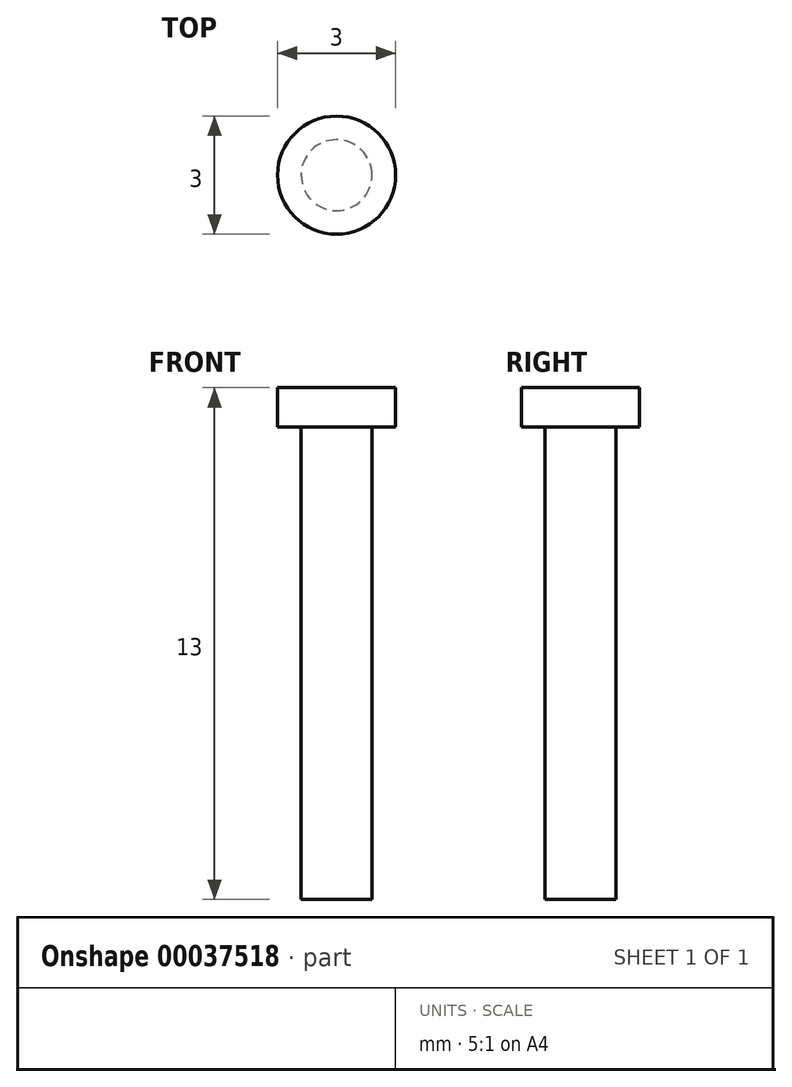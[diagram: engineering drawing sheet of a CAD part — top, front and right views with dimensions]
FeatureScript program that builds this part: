
annotation { "Feature Type Name" : "Feature", "Feature Type Description" : "" }
export const myFeature = defineFeature(function(context is Context, id is Id, definition is map)
    precondition{}
    {
        {
            var Q0;
            Q0=qCreatedBy(makeId("Top.planeOp"),FACE);
            var sketch = newSketch(context, id + "F0", { "sketchPlane" : qUnion([Q0])});
            skCircle(sketch, "E0", {"center": v(0, 0) * mm, "radius": 1.5 * mm});
            skCircle(sketch, "E1", {"center": v(0, 0) * mm, "radius": 0.9 * mm});
            skSolve(sketch);
        }
        {
            var Q0;
            Q0=makeQuery(id+"F0.imprint","IMPRINT",FACE,{"disambiguationData":[TD([[makeQuery(id+"F0.imprint","IMPRINT",EDGE,{"derivedFrom":sQuery(id+"F0.wireOp",EDGE,"E1")}),1.0]])]});
            var Q1;
            Q1=sQuery(id+"F0.wireOp",EDGE,"E1");
            extrude(context, id + "F1", {"entities" : qUnion([Q0]), "surfaceEntities" : qUnion([Q1]), "oppositeDirection" : true, "depth" : 12 * mm});
        }
        {
            var Q0;
            Q0=qSketchRegion(id+"F0",true);
            extrude(context, id + "F2", {"entities" : qUnion([Q0]), "depth" : 1 * mm});
        }
        {
            var Q0;
            Q0=makeQuery(id+"F1.opExtrude","CAP_FACE",FACE,{"disambiguationData":[OSD([sQuery(id+"F0.wireOp",EDGE,"E1")])],"isStart":true});
            var Q1;
            Q1=makeQuery(id+"F2.opExtrude","CAP_FACE",FACE,{"disambiguationData":[OSD([sQuery(id+"F0.wireOp",EDGE,"E0"),sQuery(id+"F0.wireOp",EDGE,"E1")])],"isStart":false});
            extrude(context, id + "F3", {"entities" : qUnion([Q0]), "operationType" : NewBodyOperationType.ADD, "endBound" : BoundingType.UP_TO_SURFACE, "endBoundEntityFace" : qUnion([Q1]), "depth" : 25 * mm});
        }
    });
